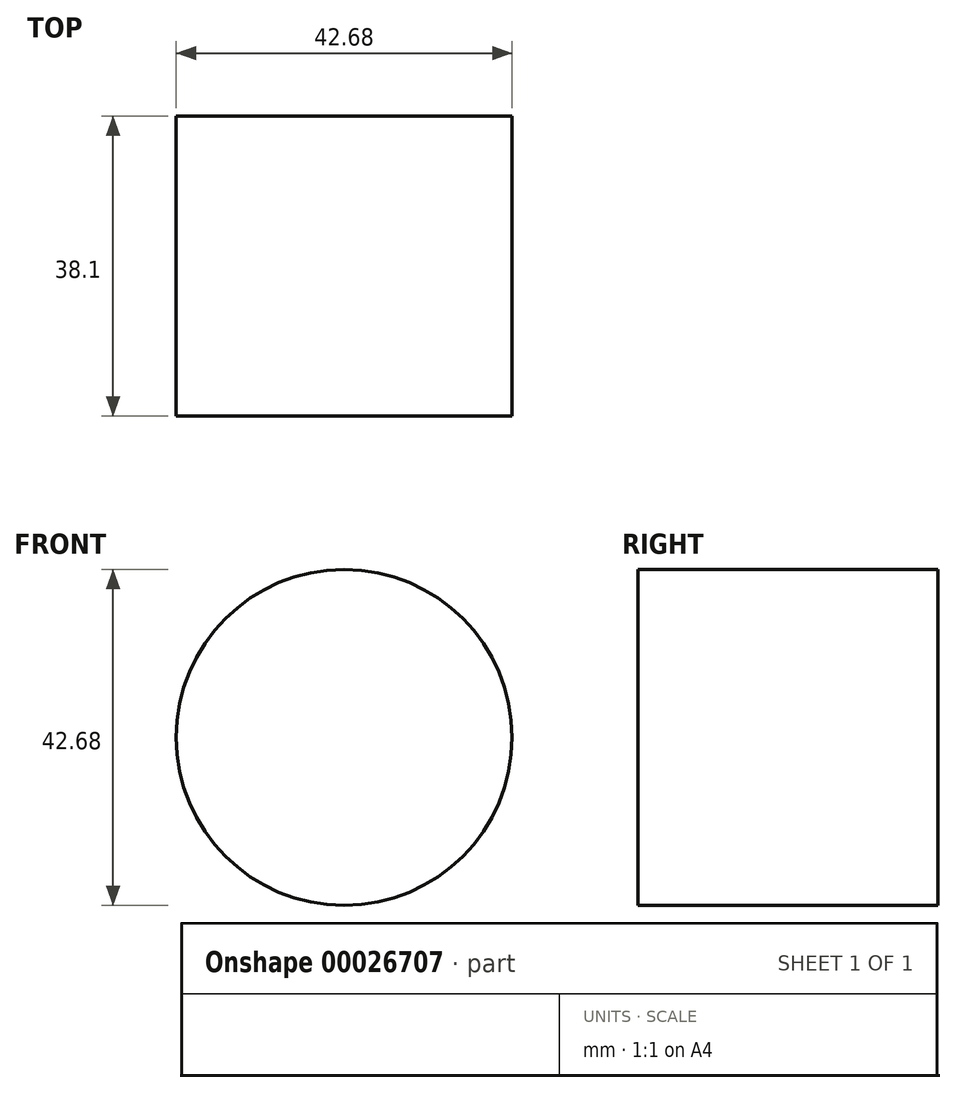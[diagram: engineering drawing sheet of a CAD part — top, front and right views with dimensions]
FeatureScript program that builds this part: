
annotation { "Feature Type Name" : "Feature", "Feature Type Description" : "" }
export const myFeature = defineFeature(function(context is Context, id is Id, definition is map)
    precondition{}
    {
        {
            var Q0;
            Q0=qCreatedBy(makeId("Front.planeOp"),FACE);
            var sketch = newSketch(context, id + "F0", { "sketchPlane" : qUnion([Q0])});
            skCircle(sketch, "E0", {"center": v(0, 0) * mm, "radius": 21.34 * mm});
            skSolve(sketch);
        }
        {
            var Q0;
            Q0=makeQuery(id+"F0.imprint","IMPRINT",FACE,{"disambiguationData":[TD([[makeQuery(id+"F0.imprint","IMPRINT",EDGE,{"derivedFrom":sQuery(id+"F0.wireOp",EDGE,"E0")}),1.0]])]});
            extrude(context, id + "F1", {"entities" : qUnion([Q0]), "depth" : 38.1 * mm});
        }
    });
